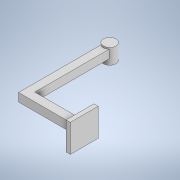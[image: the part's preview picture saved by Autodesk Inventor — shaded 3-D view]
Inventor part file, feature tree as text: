
AUTODESK INVENTOR PART (.ipt)
format: ipt  version: 2020.2 (Build 242310000, 310)  size: 172,032 bytes
history: native  units: in
note: dims shown in document units (in); Inventor stores cm internally (conversion verified against a paired STEP export)
features: extrude x6, sketch x6, projected_geometry x2
ambient origin geometry x8: Origin, YZ Plane, XZ Plane, XY Plane, X Axis, Y Axis, Z Axis, Center Point
bodies: Body1 (feature_tree)
feature tree (14):
  extrude  "Extrusion2"  Depth=0.2047in
  extrude  "Extrusion3"  Depth=0.0394in
  extrude  "Extrusion4"  Depth=0.0394in TaperAngle=0.0deg
  extrude  "Extrusion7"  Depth=0.1181in
  extrude  "Extrusion8"  Depth=0.1181in
  extrude  "Extrusion11"  Depth=0.2362in
  sketch  "Sketch3"  dims[d10=0.3543in d11=0.2047in]
  sketch  "Sketch4"  dims[d12=0.1575in d13=0.0in d14=0.0394in]
  projected_geometry  "Projected Loop1"
  sketch  "Sketch5"  dims[d16=0.2362in d17=0.0in d18=0.0394in d19=0.0in]
  sketch  "Sketch6"  dims[d20=0.0394in d21=0.1181in]
  sketch  "Sketch8"  dims[d22=90.0deg d32=0.1181in]
  projected_geometry  "Projected Loop2"
  sketch  "Sketch11"  dims[d33=180.0deg d34=0.2362in d35=90.0deg d36=0.2362in d37=90.0deg d38=2.4094in d39=0.0in d40=0.2362in d41=1.4in d42=0.0in d59=0.2755in d60=0.276in d61=0.787in d62=0.787in d63=0.1181in d64=0.0in]
